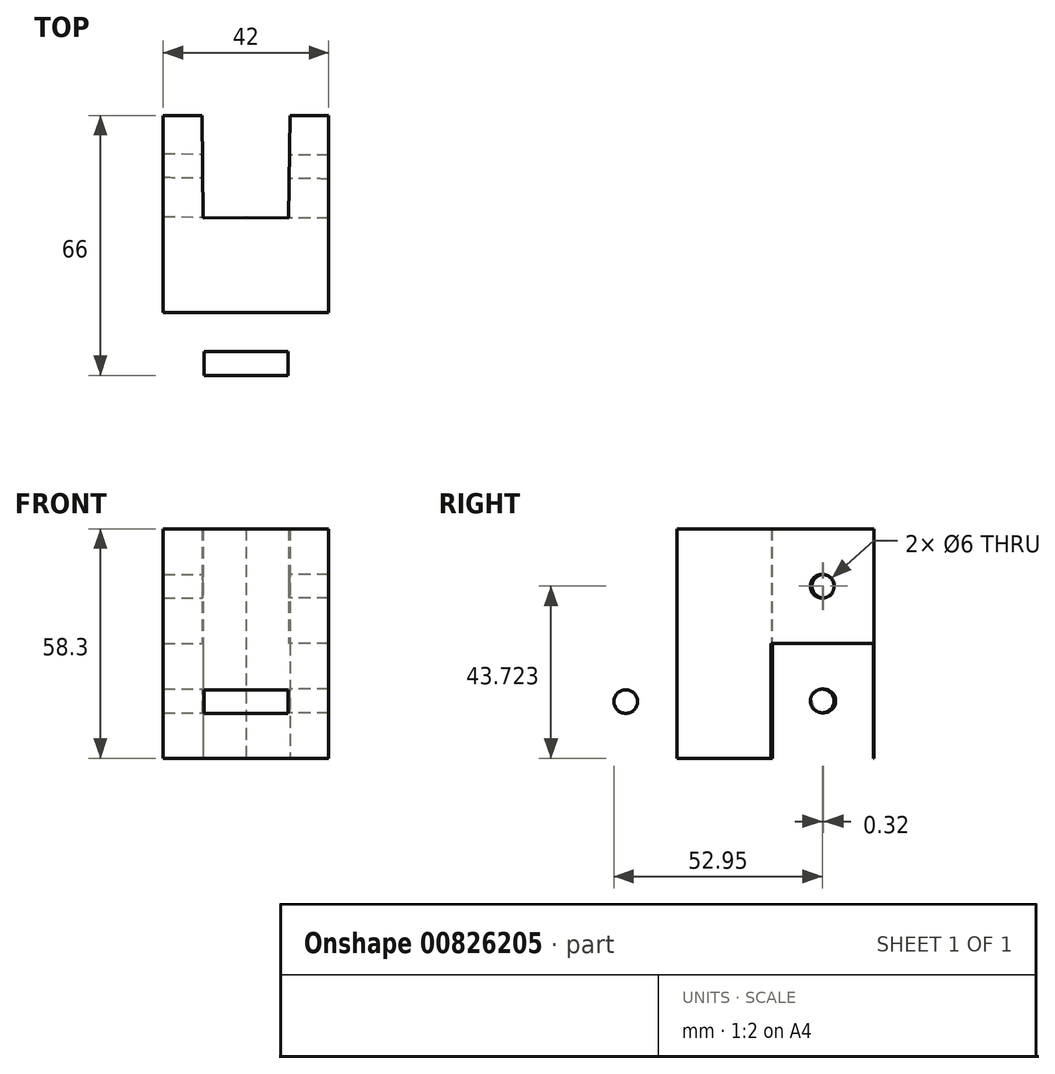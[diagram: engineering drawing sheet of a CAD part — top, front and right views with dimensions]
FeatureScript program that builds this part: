
annotation { "Feature Type Name" : "Feature", "Feature Type Description" : "" }
export const myFeature = defineFeature(function(context is Context, id is Id, definition is map)
    precondition{}
    {
        {
            var Q0;
            Q0=qCreatedBy(makeId("Top.planeOp"),FACE);
            var sketch = newSketch(context, id + "F0", { "sketchPlane" : qUnion([Q0])});
            skLineSegment(sketch, "E0.bottom", {"start": v(-10.64, -26) * mm, "end": v(10.64, -26) * mm});
            skLineSegment(sketch, "E0.left", {"start": v(-10.63, -26) * mm, "end": v(-10.63, 0) * mm});
            skLineSegment(sketch, "E0.right", {"start": v(10.64, -26) * mm, "end": v(10.64, 0) * mm});
            skLineSegment(sketch, "E1.bottom", {"start": v(-21, 50) * mm, "end": v(-11.14, 50) * mm});
            skLineSegment(sketch, "E1.top", {"start": v(-21, 0) * mm, "end": v(-10.63, 0) * mm});
            skLineSegment(sketch, "E1.left", {"start": v(-21, 50) * mm, "end": v(-21, 0) * mm});
            skLineSegment(sketch, "E1.right", {"start": v(21, 50) * mm, "end": v(21, 0) * mm});
            skLineSegment(sketch, "E2", {"start": v(11.14, 50) * mm, "end": v(10.88, 24) * mm});
            skLineSegment(sketch, "E3", {"start": v(10.88, 24) * mm, "end": v(0, 24.1) * mm});
            skLineSegment(sketch, "E4.MirrorCS", {"start": v(-10.88, 24) * mm, "end": v(0, 24.1) * mm});
            skLineSegment(sketch, "E5.MirrorCS", {"start": v(-10.88, 24) * mm, "end": v(-11.14, 50) * mm, "construction": true});
            skLineSegment(sketch, "E6.MirrorCS", {"start": v(-11.14, 50) * mm, "end": v(-10.88, 24) * mm});
            skPoint(sketch, "E7.orphan", {"position": v(-10.63, 0) * mm});
            skLineSegment(sketch, "E8.trimOffspring", {"start": v(11.14, 50) * mm, "end": v(21, 50) * mm});
            skLineSegment(sketch, "E9.trimOffspring", {"start": v(10.64, 0) * mm, "end": v(21, 0) * mm});
            skSolve(sketch);
        }
        {
            var Q0;
            Q0=makeQuery(id+"F0.imprint","IMPRINT",FACE,{"disambiguationData":[TD([[makeQuery(id+"F0.imprint","IMPRINT",EDGE,{"derivedFrom":sQuery(id+"F0.wireOp",EDGE,"E0.bottom")}),1.0]])]});
            extrude(context, id + "F1", {"entities" : qUnion([Q0]), "depth" : 58.3 * mm, "offsetDistance" : 25 * mm});
        }
        {
            var Q0;
            Q0=makeQuery(id+"F1.opExtrude","SWEPT_FACE",FACE,{"disambiguationData":[OSD([sQuery(id+"F0.wireOp",EDGE,"E0.left")])]});
            var sketch = newSketch(context, id + "F2", { "sketchPlane" : qUnion([Q0])});
            skLineSegment(sketch, "E10", {"start": v(0, 29.15) * mm, "end": v(26, 29.15) * mm, "construction": true});
            skCircle(sketch, "E11", {"center": v(13, 43.9) * mm, "radius": 3 * mm});
            skLineSegment(sketch, "E12", {"start": v(26, 29.15) * mm, "end": v(26, 58.3) * mm, "construction": true});
            skCircle(sketch, "E13.MirrorC", {"center": v(13, 14.4) * mm, "radius": 3 * mm});
            skSolve(sketch);
        }
        {
            var Q0;
            Q0=makeQuery(id+"F2.imprint","IMPRINT",FACE,{"disambiguationData":[TD([[makeQuery(id+"F2.imprint","IMPRINT",EDGE,{"derivedFrom":sQuery(id+"F2.wireOp",EDGE,"E13.MirrorC")}),-1.0]])]});
            var Q1;
            Q1=makeQuery(id+"F2.imprint","IMPRINT",FACE,{"disambiguationData":[TD([[makeQuery(id+"F2.imprint","IMPRINT",EDGE,{"derivedFrom":sQuery(id+"F2.wireOp",EDGE,"E11")}),1.0]])]});
            extrude(context, id + "F3", {"entities" : qUnion([Q0, Q1]), "operationType" : NewBodyOperationType.REMOVE, "oppositeDirection" : true, "depth" : 25 * mm, "offsetDistance" : 25 * mm});
        }
        {
            var Q0;
            Q0=makeQuery(id+"F1.opExtrude","SWEPT_FACE",FACE,{"disambiguationData":[OSD([sQuery(id+"F0.wireOp",EDGE,"E2")])]});
            var sketch = newSketch(context, id + "F4", { "sketchPlane" : qUnion([Q0])});
            skLineSegment(sketch, "E14", {"start": v(-50.1, 29.15) * mm, "end": v(-24.1, 29.15) * mm});
            skCircle(sketch, "E15", {"center": v(-37.1, 43.72) * mm, "radius": 3 * mm});
            skPoint(sketch, "E16.start.orphan", {"position": v(-37.1, 29.15) * mm});
            skLineSegment(sketch, "E17", {"start": v(-50.1, 43.72) * mm, "end": v(-24.1, 43.72) * mm, "construction": true});
            skCircle(sketch, "E18.MirrorC", {"center": v(-37.1, 14.58) * mm, "radius": 3 * mm});
            skSolve(sketch);
        }
        {
            var Q0;
            Q0=makeQuery(id+"F4.imprint","IMPRINT",FACE,{"disambiguationData":[TD([[makeQuery(id+"F4.imprint","IMPRINT",EDGE,{"derivedFrom":sQuery(id+"F4.wireOp",EDGE,"E18.MirrorC")}),-1.0]])]});
            var Q1;
            Q1=makeQuery(id+"F4.imprint","IMPRINT",FACE,{"disambiguationData":[TD([[makeQuery(id+"F4.imprint","IMPRINT",EDGE,{"derivedFrom":sQuery(id+"F4.wireOp",EDGE,"E15")}),1.0]])]});
            extrude(context, id + "F5", {"entities" : qUnion([Q0, Q1]), "operationType" : NewBodyOperationType.REMOVE, "oppositeDirection" : true, "depth" : 25 * mm, "offsetDistance" : 25 * mm});
        }
        {
            var Q0;
            Q0=makeQuery(id+"F4.imprint","IMPRINT",FACE,{"disambiguationData":[TD([[makeQuery(id+"F4.imprint","IMPRINT",EDGE,{"derivedFrom":sQuery(id+"F4.wireOp",EDGE,"E15")}),1.0]])]});
            var Q1;
            Q1=makeQuery(id+"F4.imprint","IMPRINT",FACE,{"disambiguationData":[TD([[makeQuery(id+"F4.imprint","IMPRINT",EDGE,{"derivedFrom":sQuery(id+"F4.wireOp",EDGE,"E18.MirrorC")}),-1.0]])]});
            extrude(context, id + "F6", {"entities" : qUnion([Q0, Q1]), "operationType" : NewBodyOperationType.REMOVE, "depth" : 100 * mm, "offsetDistance" : 25 * mm});
        }
    });
